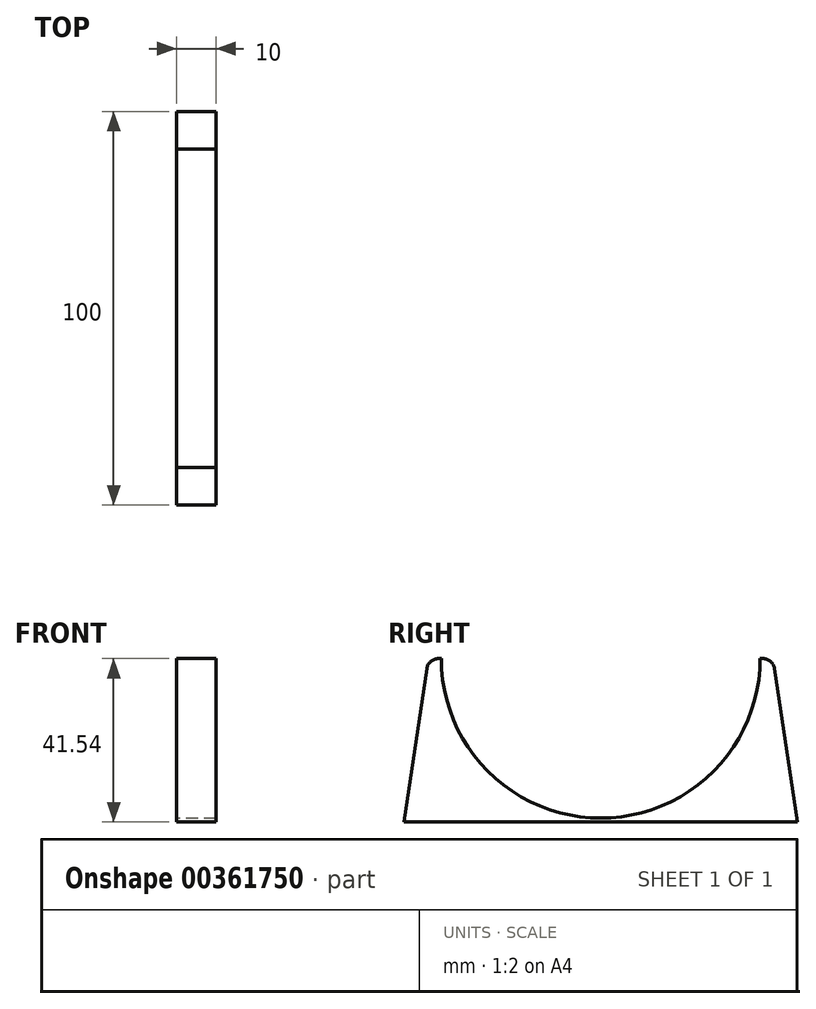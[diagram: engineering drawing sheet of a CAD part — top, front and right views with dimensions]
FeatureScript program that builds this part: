
annotation { "Feature Type Name" : "Feature", "Feature Type Description" : "" }
export const myFeature = defineFeature(function(context is Context, id is Id, definition is map)
    precondition{}
    {
        {
            var Q0;
            Q0=qCreatedBy(makeId("Right.planeOp"),FACE);
            var sketch = newSketch(context, id + "F0", { "sketchPlane" : qUnion([Q0])});
            skArc(sketch, "E0", {"start": v(-40.5, 0.04) * mm, "mid": v(-28.65, -28.62) * mm, "end": v(0, -40.5) * mm});
            skLineSegment(sketch, "E1", {"start": v(-43.8, 0.04) * mm, "end": v(-40.5, 0.04) * mm});
            skLineSegment(sketch, "E2", {"start": v(0, -41.5) * mm, "end": v(0, 43.5) * mm});
            skLineSegment(sketch, "E3", {"start": v(-43.8, 0.04) * mm, "end": v(-50, -41.5) * mm});
            skLineSegment(sketch, "E4", {"start": v(-50, -41.5) * mm, "end": v(0, -41.5) * mm});
            skPoint(sketch, "E5.0.center.orphan", {"position": v(-0.3, 0.04) * mm});
            skLineSegment(sketch, "E6.MirrorCS", {"start": v(43.8, 0.04) * mm, "end": v(40.5, 0.04) * mm});
            skArc(sketch, "E7.MirrorCS", {"start": v(40.5, 0.04) * mm, "mid": v(28.65, -28.62) * mm, "end": v(0, -40.5) * mm});
            skLineSegment(sketch, "E8.MirrorCS", {"start": v(50, -41.5) * mm, "end": v(0, -41.5) * mm});
            skLineSegment(sketch, "E9.MirrorCS", {"start": v(43.8, 0.04) * mm, "end": v(50, -41.5) * mm});
            skSolve(sketch);
        }
        {
            var Q0;
            {var subQ1=sQuery(id+"F0.wireOp",EDGE,"E0");Q0=makeQuery(id+"F0.imprint","IMPRINT",FACE,{"disambiguationData":[TD([[makeQuery(id+"F0.imprint","IMPRINT",EDGE,{"derivedFrom":subQ1}),-1.0]])]});}
            var Q1;
            Q1=makeQuery(id+"F0.imprint","IMPRINT",FACE,{"disambiguationData":[TD([[makeQuery(id+"F0.imprint","IMPRINT",EDGE,{"derivedFrom":sQuery(id+"F0.wireOp",EDGE,"E6.MirrorCS")}),1.0]])]});
            extrude(context, id + "F1", {"entities" : qUnion([Q0, Q1]), "depth" : 10 * mm, "offsetDistance" : 25 * mm});
        }
        {
            var Q0;
            Q0=makeQuery(id+"F1.opExtrude","SWEPT_EDGE",EDGE,{"disambiguationData":[OSD([sQuery(id+"F0.wireOp",EDGE,"E1"),sQuery(id+"F0.wireOp",EDGE,"E3")])]});
            var Q1;
            Q1=makeQuery(id+"F1.opExtrude","SWEPT_EDGE",EDGE,{"disambiguationData":[OSD([sQuery(id+"F0.wireOp",EDGE,"E6.MirrorCS"),sQuery(id+"F0.wireOp",EDGE,"E9.MirrorCS")])]});
            fillet(context, id + "F2", {"entities" : qUnion([Q0, Q1]), "radius" : 3 * mm, "tangentPropagation" : true, "allowEdgeOverflow" : false});
        }
    });
